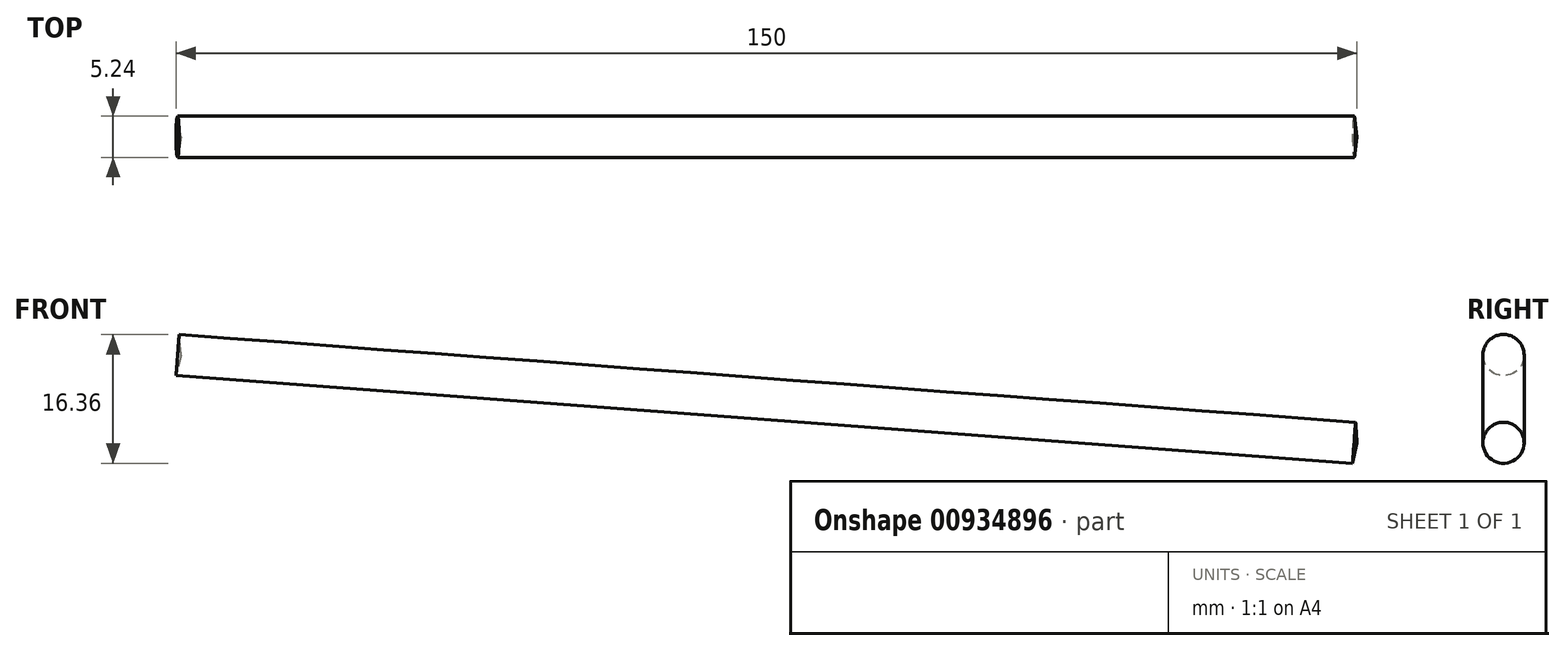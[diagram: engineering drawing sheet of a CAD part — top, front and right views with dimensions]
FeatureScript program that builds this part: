
annotation { "Feature Type Name" : "Feature", "Feature Type Description" : "" }
export const myFeature = defineFeature(function(context is Context, id is Id, definition is map)
    precondition{}
    {
        {
            var Q0;
            Q0=qCreatedBy(makeId("Front.planeOp"),FACE);
            var sketch = newSketch(context, id + "F0", { "sketchPlane" : qUnion([Q0])});
            skLineSegment(sketch, "E0", {"start": v(-149.35, 11.14) * mm, "end": v(0, 0) * mm});
            skLineSegment(sketch, "E1", {"start": v(0, 0) * mm, "end": v(-0.56, -2.58) * mm});
            skLineSegment(sketch, "E2", {"start": v(-0.56, -2.58) * mm, "end": v(-150, 8.56) * mm});
            skLineSegment(sketch, "E3", {"start": v(-150, 8.56) * mm, "end": v(-149.35, 11.14) * mm});
            skSolve(sketch);
        }
        {
            var Q0;
            Q0=makeQuery(id+"F0.imprint","IMPRINT",FACE,{"disambiguationData":[TD([[makeQuery(id+"F0.imprint","IMPRINT",EDGE,{"derivedFrom":sQuery(id+"F0.wireOp",EDGE,"E0")}),-1.0]])]});
            var Q1;
            Q1=sQuery(id+"F0.wireOp",EDGE,"E0");
            revolve(context, id + "F1", {"surfaceOperationType" : NewSurfaceOperationType.NEW, "entities" : qUnion([Q0]), "axis" : qUnion([Q1]), "revolveType" : RevolveType.FULL});
        }
    });
